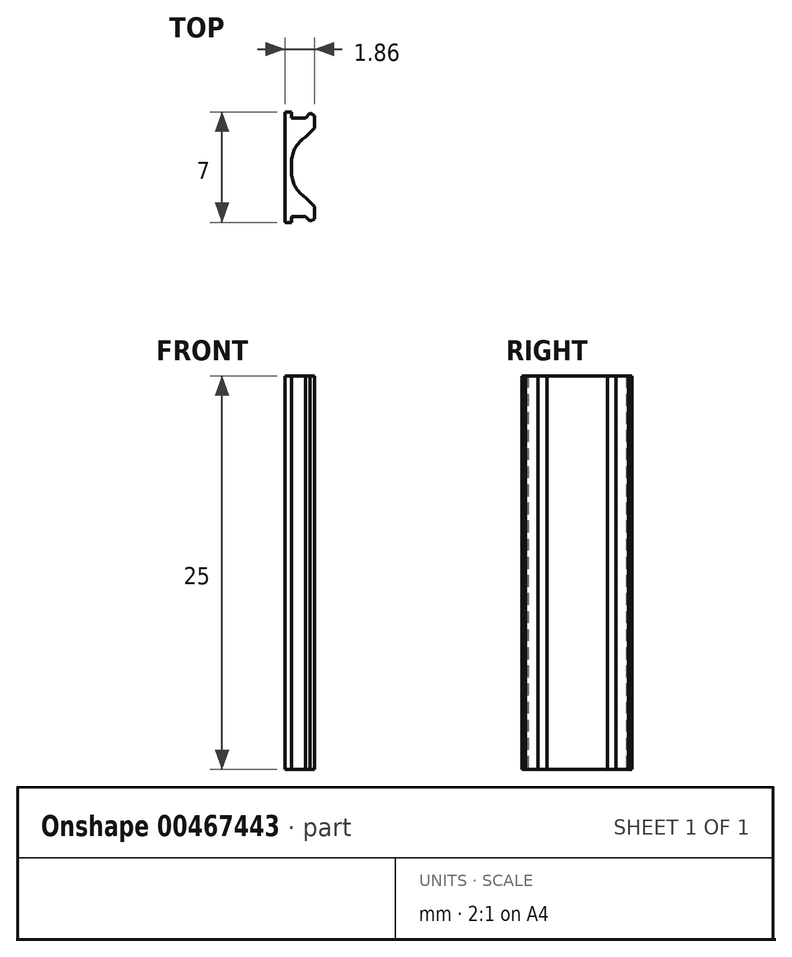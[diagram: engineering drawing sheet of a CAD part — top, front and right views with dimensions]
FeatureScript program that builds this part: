
annotation { "Feature Type Name" : "Feature", "Feature Type Description" : "" }
export const myFeature = defineFeature(function(context is Context, id is Id, definition is map)
    precondition{}
    {
        {
            var Q0;
            Q0=qCreatedBy(makeId("Top.planeOp"),FACE);
            var sketch = newSketch(context, id + "F0", { "sketchPlane" : qUnion([Q0])});
            skLineSegment(sketch, "E0", {"start": v(-7.23, 3.5) * mm, "end": v(-6.83, 3.5) * mm});
            skLineSegment(sketch, "E1", {"start": v(-6.83, 3.5) * mm, "end": v(-6.83, 3.12) * mm});
            skLineSegment(sketch, "E2", {"start": v(-6.83, 3.12) * mm, "end": v(-5.93, 3.12) * mm});
            skLineSegment(sketch, "E3", {"start": v(-5.93, 3.12) * mm, "end": v(-5.63, 3.42) * mm});
            skLineSegment(sketch, "E4", {"start": v(-5.63, 3.42) * mm, "end": v(-5.37, 3.27) * mm});
            skLineSegment(sketch, "E5", {"start": v(-5.37, 3.27) * mm, "end": v(-5.37, 2.48) * mm});
            skLineSegment(sketch, "E6", {"start": v(-7.23, 0) * mm, "end": v(-7.23, 3.5) * mm});
            skLineSegment(sketch, "E7", {"start": v(-6.83, -0.6) * mm, "end": v(-6.83, 1.92) * mm});
            skLineSegment(sketch, "E8", {"start": v(-6.83, 1.92) * mm, "end": v(-5.93, 1.92) * mm});
            skPoint(sketch, "E9.orphan", {"position": v(-5.37, 0) * mm});
            skLineSegment(sketch, "E10.MirrorCS", {"start": v(-5.93, -3.12) * mm, "end": v(-5.63, -3.42) * mm});
            skLineSegment(sketch, "E11.MirrorCS", {"start": v(-5.63, -3.42) * mm, "end": v(-5.37, -3.28) * mm});
            skLineSegment(sketch, "E12.MirrorCS", {"start": v(-6.83, -3.12) * mm, "end": v(-5.93, -3.12) * mm});
            skLineSegment(sketch, "E13.MirrorCS", {"start": v(-7.23, -3.5) * mm, "end": v(-6.83, -3.5) * mm});
            skLineSegment(sketch, "E14.MirrorCS", {"start": v(-5.37, -3.27) * mm, "end": v(-5.37, -2.48) * mm});
            skLineSegment(sketch, "E15.MirrorCS", {"start": v(-7.23, 0) * mm, "end": v(-7.23, -3.5) * mm});
            skLineSegment(sketch, "E16.MirrorCS", {"start": v(-6.83, 0.6) * mm, "end": v(-6.83, -1.92) * mm});
            skLineSegment(sketch, "E17.MirrorCS", {"start": v(-6.83, -1.92) * mm, "end": v(-5.93, -1.92) * mm});
            skLineSegment(sketch, "E18.MirrorCS", {"start": v(-6.83, -3.5) * mm, "end": v(-6.83, -3.12) * mm});
            skLineSegment(sketch, "E19", {"start": v(-5.37, 2.48) * mm, "end": v(-5.93, 1.92) * mm});
            skLineSegment(sketch, "E20.MirrorCS", {"start": v(-5.37, -2.48) * mm, "end": v(-5.93, -1.92) * mm});
            skPoint(sketch, "E21.orphan", {"position": v(-5.37, 1.93) * mm});
            skPoint(sketch, "E22.orphan", {"position": v(-5.37, -1.93) * mm});
            skSolve(sketch);
        }
        {
            var Q0;
            Q0=makeQuery(id+"F0.imprint","IMPRINT",FACE,{"disambiguationData":[TD([[makeQuery(id+"F0.imprint","IMPRINT",EDGE,{"derivedFrom":sQuery(id+"F0.wireOp",EDGE,"E0")}),-1.0]])]});
            extrude(context, id + "F1", {"entities" : qUnion([Q0]), "depth" : 25 * mm});
        }
        {
            var Q0;
            Q0=makeQuery(id+"F1.opExtrude","SWEPT_EDGE",EDGE,{"disambiguationData":[OSD([sQuery(id+"F0.wireOp",EDGE,"E7"),sQuery(id+"F0.wireOp",EDGE,"E8")])]});
            var Q1;
            Q1=makeQuery(id+"F1.opExtrude","SWEPT_EDGE",EDGE,{"disambiguationData":[OSD([sQuery(id+"F0.wireOp",EDGE,"E16.MirrorCS"),sQuery(id+"F0.wireOp",EDGE,"E17.MirrorCS")])]});
            fillet(context, id + "F2", {"entities" : qUnion([Q0, Q1]), "radius" : 2 * mm, "tangentPropagation" : true, "allowEdgeOverflow" : false});
        }
    });
